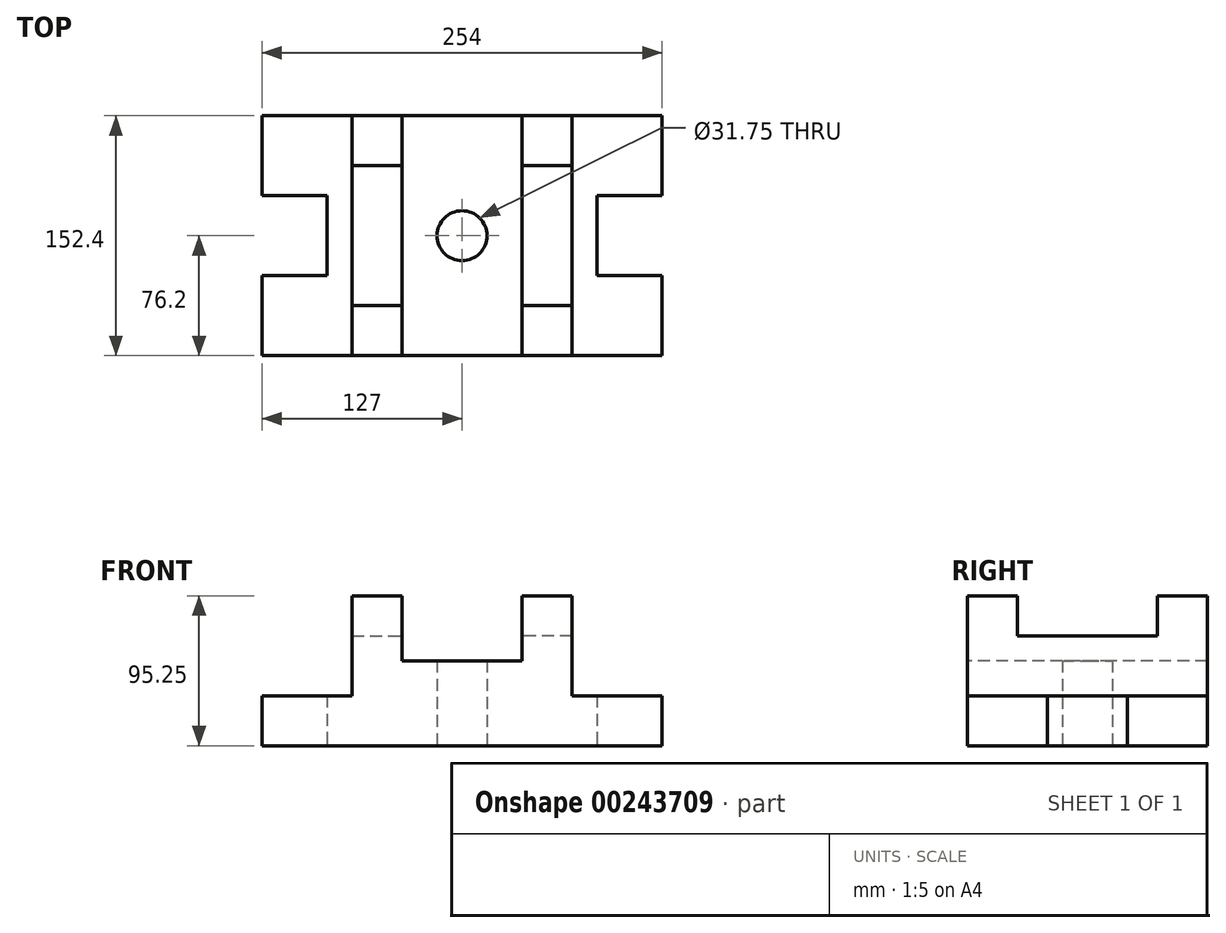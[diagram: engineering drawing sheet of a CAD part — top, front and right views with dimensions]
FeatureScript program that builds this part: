
annotation { "Feature Type Name" : "Feature", "Feature Type Description" : "" }
export const myFeature = defineFeature(function(context is Context, id is Id, definition is map)
    precondition{}
    {
        {
            var Q0;
            Q0=qCreatedBy(makeId("Top.planeOp"),FACE);
            var sketch = newSketch(context, id + "F0", { "sketchPlane" : qUnion([Q0])});
            skCircle(sketch, "E0", {"center": v(0, 0) * mm, "radius": 15.88 * mm});
            skLineSegment(sketch, "E1", {"start": v(0, -76.2) * mm, "end": v(127, -76.2) * mm});
            skLineSegment(sketch, "E2", {"start": v(0, -76.2) * mm, "end": v(-127, -76.2) * mm});
            skLineSegment(sketch, "E3", {"start": v(0, 76.2) * mm, "end": v(127, 76.2) * mm});
            skLineSegment(sketch, "E4", {"start": v(0, 76.2) * mm, "end": v(-127, 76.2) * mm});
            skLineSegment(sketch, "E5", {"start": v(-127, 76.2) * mm, "end": v(-127, 25.4) * mm});
            skLineSegment(sketch, "E6", {"start": v(127, 76.2) * mm, "end": v(127, 25.4) * mm});
            skLineSegment(sketch, "E7", {"start": v(-127, -76.2) * mm, "end": v(-127, -25.4) * mm});
            skLineSegment(sketch, "E8", {"start": v(-127, 25.4) * mm, "end": v(-85.73, 25.4) * mm});
            skLineSegment(sketch, "E9", {"start": v(-85.73, 25.4) * mm, "end": v(-85.73, -25.37) * mm});
            skLineSegment(sketch, "E10", {"start": v(-85.72, -25.37) * mm, "end": v(-127, -25.4) * mm});
            skLineSegment(sketch, "E11.trimOffspring", {"start": v(-127, -25.4) * mm, "end": v(-127, -76.2) * mm});
            skLineSegment(sketch, "E12", {"start": v(127, 25.4) * mm, "end": v(85.72, 25.4) * mm});
            skLineSegment(sketch, "E13", {"start": v(85.72, 25.4) * mm, "end": v(85.72, -25.4) * mm});
            skLineSegment(sketch, "E14", {"start": v(85.72, -25.4) * mm, "end": v(127, -25.4) * mm});
            skLineSegment(sketch, "E15.trimOffspring", {"start": v(127, -25.4) * mm, "end": v(127, -76.2) * mm});
            skSolve(sketch);
        }
        {
            var Q0;
            Q0=makeQuery(id+"F0.imprint","IMPRINT",FACE,{"disambiguationData":[TD([[makeQuery(id+"F0.imprint","IMPRINT",EDGE,{"derivedFrom":sQuery(id+"F0.wireOp",EDGE,"E0")}),-1.0]])]});
            extrude(context, id + "F1", {"entities" : qUnion([Q0]), "depth" : 31.75 * mm});
        }
        {
            var Q0;
            Q0=makeQuery(id+"F1.opExtrude","CAP_FACE",FACE,{"disambiguationData":[OSD([sQuery(id+"F0.wireOp",EDGE,"E0"),sQuery(id+"F0.wireOp",EDGE,"E1"),sQuery(id+"F0.wireOp",EDGE,"E2"),sQuery(id+"F0.wireOp",EDGE,"E3"),sQuery(id+"F0.wireOp",EDGE,"E4"),sQuery(id+"F0.wireOp",EDGE,"E5"),sQuery(id+"F0.wireOp",EDGE,"E8"),sQuery(id+"F0.wireOp",EDGE,"E9"),sQuery(id+"F0.wireOp",EDGE,"E10"),sQuery(id+"F0.wireOp",EDGE,"E11.trimOffspring"),sQuery(id+"F0.wireOp",EDGE,"E6"),sQuery(id+"F0.wireOp",EDGE,"E12"),sQuery(id+"F0.wireOp",EDGE,"E13"),sQuery(id+"F0.wireOp",EDGE,"E14"),sQuery(id+"F0.wireOp",EDGE,"E15.trimOffspring")])],"isStart":false});
            var sketch = newSketch(context, id + "F2", { "sketchPlane" : qUnion([Q0])});
            skLineSegment(sketch, "E16", {"start": v(-127, -76.2) * mm, "end": v(-69.85, -76.2) * mm});
            skLineSegment(sketch, "E17", {"start": v(127, -76.2) * mm, "end": v(69.85, -76.2) * mm});
            skLineSegment(sketch, "E18", {"start": v(-69.85, -76.2) * mm, "end": v(-69.85, 76.2) * mm});
            skLineSegment(sketch, "E19", {"start": v(69.85, -76.2) * mm, "end": v(69.85, 76.2) * mm});
            skSolve(sketch);
        }
        {
            var Q0;
            {var subQ0=sQuery(id+"F2.wireOp",EDGE,"E18");Q0=makeQuery(id+"F2.imprint","IMPRINT",FACE,{"disambiguationData":[TD([[makeQuery(id+"F2.imprint","IMPRINT",EDGE,{"derivedFrom":subQ0}),-1.0]])]});}
            extrude(context, id + "F3", {"entities" : qUnion([Q0]), "operationType" : NewBodyOperationType.ADD, "depth" : 22.22 * mm});
        }
        {
            var Q0;
            Q0=makeQuery(id+"F3.opExtrude","CAP_FACE",FACE,{"disambiguationData":[OSD([sQuery(id+"F0.wireOp",EDGE,"E0"),sQuery(id+"F0.wireOp",EDGE,"E1"),sQuery(id+"F0.wireOp",EDGE,"E2"),sQuery(id+"F0.wireOp",EDGE,"E3"),sQuery(id+"F0.wireOp",EDGE,"E4"),sQuery(id+"F2.wireOp",EDGE,"E18"),sQuery(id+"F2.wireOp",EDGE,"E19")])],"isStart":false});
            var sketch = newSketch(context, id + "F4", { "sketchPlane" : qUnion([Q0])});
            skLineSegment(sketch, "E20", {"start": v(69.85, -76.2) * mm, "end": v(38.1, -76.2) * mm});
            skLineSegment(sketch, "E21", {"start": v(38.1, -76.2) * mm, "end": v(38.1, 76.2) * mm});
            skLineSegment(sketch, "E22", {"start": v(38.1, 76.2) * mm, "end": v(69.85, 76.2) * mm});
            skLineSegment(sketch, "E23", {"start": v(69.85, 76.2) * mm, "end": v(69.85, -76.2) * mm});
            skLineSegment(sketch, "E24", {"start": v(-69.85, -76.2) * mm, "end": v(-38.1, -76.2) * mm});
            skLineSegment(sketch, "E25", {"start": v(-38.1, 76.2) * mm, "end": v(-38.1, -76.2) * mm});
            skSolve(sketch);
        }
        {
            var Q0;
            Q0=makeQuery(id+"F4.imprint","IMPRINT",FACE,{"disambiguationData":[TD([[makeQuery(id+"F4.imprint","IMPRINT",EDGE,{"derivedFrom":sQuery(id+"F4.wireOp",EDGE,"E24")}),-1.0]])]});
            var Q1;
            Q1=makeQuery(id+"F4.imprint","IMPRINT",FACE,{"disambiguationData":[TD([[makeQuery(id+"F4.imprint","IMPRINT",EDGE,{"derivedFrom":sQuery(id+"F4.wireOp",EDGE,"E20")}),-1.0]])]});
            extrude(context, id + "F5", {"entities" : qUnion([Q0, Q1]), "operationType" : NewBodyOperationType.ADD, "depth" : 15.88 * mm});
        }
        {
            var Q0;
            Q0=makeQuery(id+"F5.opExtrude","CAP_FACE",FACE,{"disambiguationData":[OSD([sQuery(id+"F4.wireOp",EDGE,"E20"),sQuery(id+"F4.wireOp",EDGE,"E21"),sQuery(id+"F4.wireOp",EDGE,"E22"),sQuery(id+"F4.wireOp",EDGE,"E23")])],"isStart":false});
            var sketch = newSketch(context, id + "F6", { "sketchPlane" : qUnion([Q0])});
            skLineSegment(sketch, "E26", {"start": v(38.1, -76.2) * mm, "end": v(69.85, -76.2) * mm});
            skLineSegment(sketch, "E27", {"start": v(69.85, -76.2) * mm, "end": v(69.85, -44.45) * mm});
            skLineSegment(sketch, "E28", {"start": v(69.85, -44.45) * mm, "end": v(38.1, -44.45) * mm});
            skLineSegment(sketch, "E29", {"start": v(38.1, -44.45) * mm, "end": v(38.1, -76.2) * mm});
            skSolve(sketch);
        }
        {
            var Q0;
            Q0=makeQuery(id+"F6.imprint","IMPRINT",FACE,{"disambiguationData":[TD([[makeQuery(id+"F6.imprint","IMPRINT",EDGE,{"derivedFrom":sQuery(id+"F6.wireOp",EDGE,"E26")}),-1.0]])]});
            extrude(context, id + "F7", {"entities" : qUnion([Q0]), "operationType" : NewBodyOperationType.ADD, "depth" : 25.4 * mm});
        }
        {
            var Q0;
            Q0=makeQuery(id+"F5.opExtrude","CAP_FACE",FACE,{"disambiguationData":[OSD([sQuery(id+"F4.wireOp",EDGE,"E20"),sQuery(id+"F4.wireOp",EDGE,"E21"),sQuery(id+"F4.wireOp",EDGE,"E22"),sQuery(id+"F4.wireOp",EDGE,"E23")])],"isStart":false});
            var sketch = newSketch(context, id + "F8", { "sketchPlane" : qUnion([Q0])});
            skLineSegment(sketch, "E30", {"start": v(69.85, 76.2) * mm, "end": v(69.85, 44.45) * mm});
            skLineSegment(sketch, "E31", {"start": v(69.85, 44.45) * mm, "end": v(38.1, 44.45) * mm});
            skLineSegment(sketch, "E32", {"start": v(38.1, 44.45) * mm, "end": v(38.1, 76.2) * mm});
            skLineSegment(sketch, "E33", {"start": v(38.1, 76.2) * mm, "end": v(69.8, 75.55) * mm});
            skSolve(sketch);
        }
        {
            var Q0;
            Q0=makeQuery(id+"F8.imprint","IMPRINT",FACE,{"disambiguationData":[TD([[makeQuery(id+"F8.imprint","IMPRINT",EDGE,{"derivedFrom":sQuery(id+"F8.wireOp",EDGE,"E30")}),1.0]])]});
            extrude(context, id + "F9", {"entities" : qUnion([Q0]), "operationType" : NewBodyOperationType.ADD, "depth" : 25.4 * mm});
        }
        {
            var Q0;
            Q0=makeQuery(id+"F5.opExtrude","CAP_FACE",FACE,{"disambiguationData":[OSD([sQuery(id+"F0.wireOp",EDGE,"E3"),sQuery(id+"F0.wireOp",EDGE,"E4"),sQuery(id+"F2.wireOp",EDGE,"E18"),sQuery(id+"F4.wireOp",EDGE,"E24"),sQuery(id+"F4.wireOp",EDGE,"E25")])],"isStart":false});
            var sketch = newSketch(context, id + "F10", { "sketchPlane" : qUnion([Q0])});
            skLineSegment(sketch, "E34", {"start": v(-69.85, -76.2) * mm, "end": v(-38.1, -76.2) * mm});
            skLineSegment(sketch, "E35", {"start": v(-38.1, -76.2) * mm, "end": v(-38.1, -44.45) * mm});
            skLineSegment(sketch, "E36", {"start": v(-38.1, -44.45) * mm, "end": v(-69.85, -44.45) * mm});
            skLineSegment(sketch, "E37", {"start": v(-69.85, -44.45) * mm, "end": v(-69.85, -76.2) * mm});
            skLineSegment(sketch, "E38", {"start": v(-69.85, 76.2) * mm, "end": v(-69.85, 44.45) * mm});
            skLineSegment(sketch, "E39", {"start": v(-69.85, 44.45) * mm, "end": v(-38.1, 44.45) * mm});
            skLineSegment(sketch, "E40", {"start": v(-38.1, 44.45) * mm, "end": v(-38.1, 76.2) * mm});
            skLineSegment(sketch, "E41", {"start": v(-38.1, 76.2) * mm, "end": v(-69.85, 76.2) * mm});
            skSolve(sketch);
        }
        {
            var Q0;
            Q0 = qSketchRegion(id + "F10", true);
            extrude(context, id + "F11", {"entities" : qUnion([Q0]), "operationType" : NewBodyOperationType.ADD, "depth" : 25.4 * mm});
        }
    });
